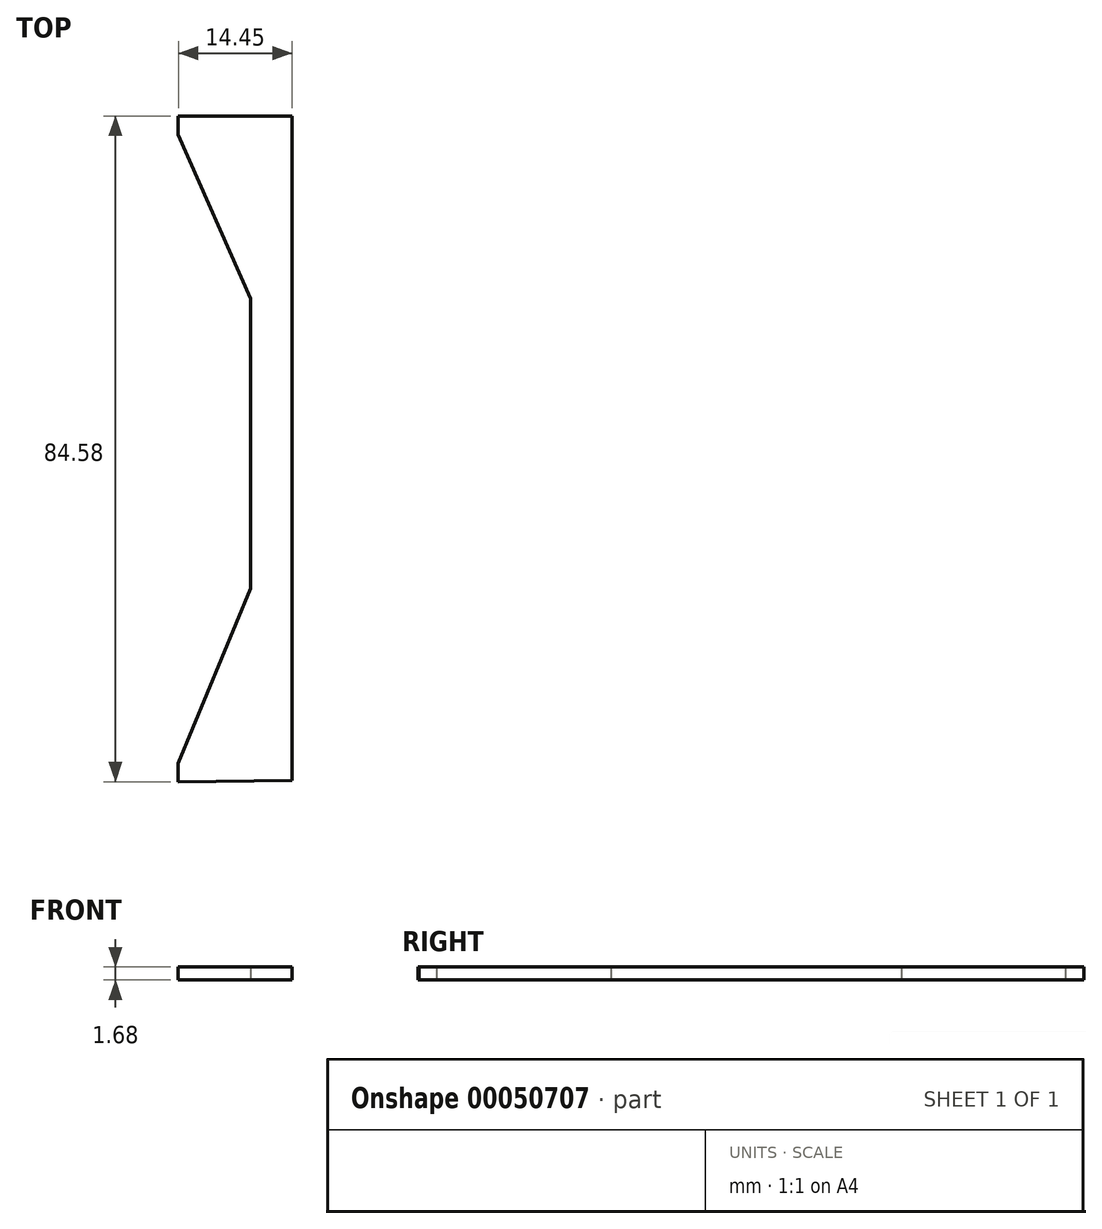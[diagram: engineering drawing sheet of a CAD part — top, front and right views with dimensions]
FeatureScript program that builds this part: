
annotation { "Feature Type Name" : "Feature", "Feature Type Description" : "" }
export const myFeature = defineFeature(function(context is Context, id is Id, definition is map)
    precondition{}
    {
        {
            var Q0;
            Q0=qCreatedBy(makeId("Top.planeOp"),FACE);
            var sketch = newSketch(context, id + "F0", { "sketchPlane" : qUnion([Q0])});
            skLineSegment(sketch, "E0", {"start": v(0, 30.66) * mm, "end": v(0, 6.89) * mm});
            skLineSegment(sketch, "E1", {"start": v(0, 6.89) * mm, "end": v(0, -30) * mm});
            skLineSegment(sketch, "E2", {"start": v(0, -30) * mm, "end": v(0, -53.77) * mm});
            skLineSegment(sketch, "E3", {"start": v(0, 30.66) * mm, "end": v(-14.45, 30.66) * mm});
            skLineSegment(sketch, "E4", {"start": v(-14.45, 30.66) * mm, "end": v(-14.45, 28.33) * mm});
            skLineSegment(sketch, "E5", {"start": v(-14.45, 28.33) * mm, "end": v(-5.27, 7.5) * mm});
            skLineSegment(sketch, "E6", {"start": v(-5.27, 7.5) * mm, "end": v(-5.27, -29.38) * mm});
            skLineSegment(sketch, "E7", {"start": v(-5.27, -29.38) * mm, "end": v(-14.45, -51.59) * mm});
            skLineSegment(sketch, "E8", {"start": v(-14.45, -51.59) * mm, "end": v(-14.45, -53.92) * mm});
            skLineSegment(sketch, "E9", {"start": v(-14.45, -53.92) * mm, "end": v(0, -53.77) * mm});
            skSolve(sketch);
        }
        {
            var Q0;
            Q0=makeQuery(id+"F0.imprint","IMPRINT",FACE,{"disambiguationData":[TD([[makeQuery(id+"F0.imprint","IMPRINT",EDGE,{"derivedFrom":sQuery(id+"F0.wireOp",EDGE,"E0")}),-1.0]])]});
            extrude(context, id + "F1", {"entities" : qUnion([Q0]), "depth" : 1.68 * mm});
        }
    });
